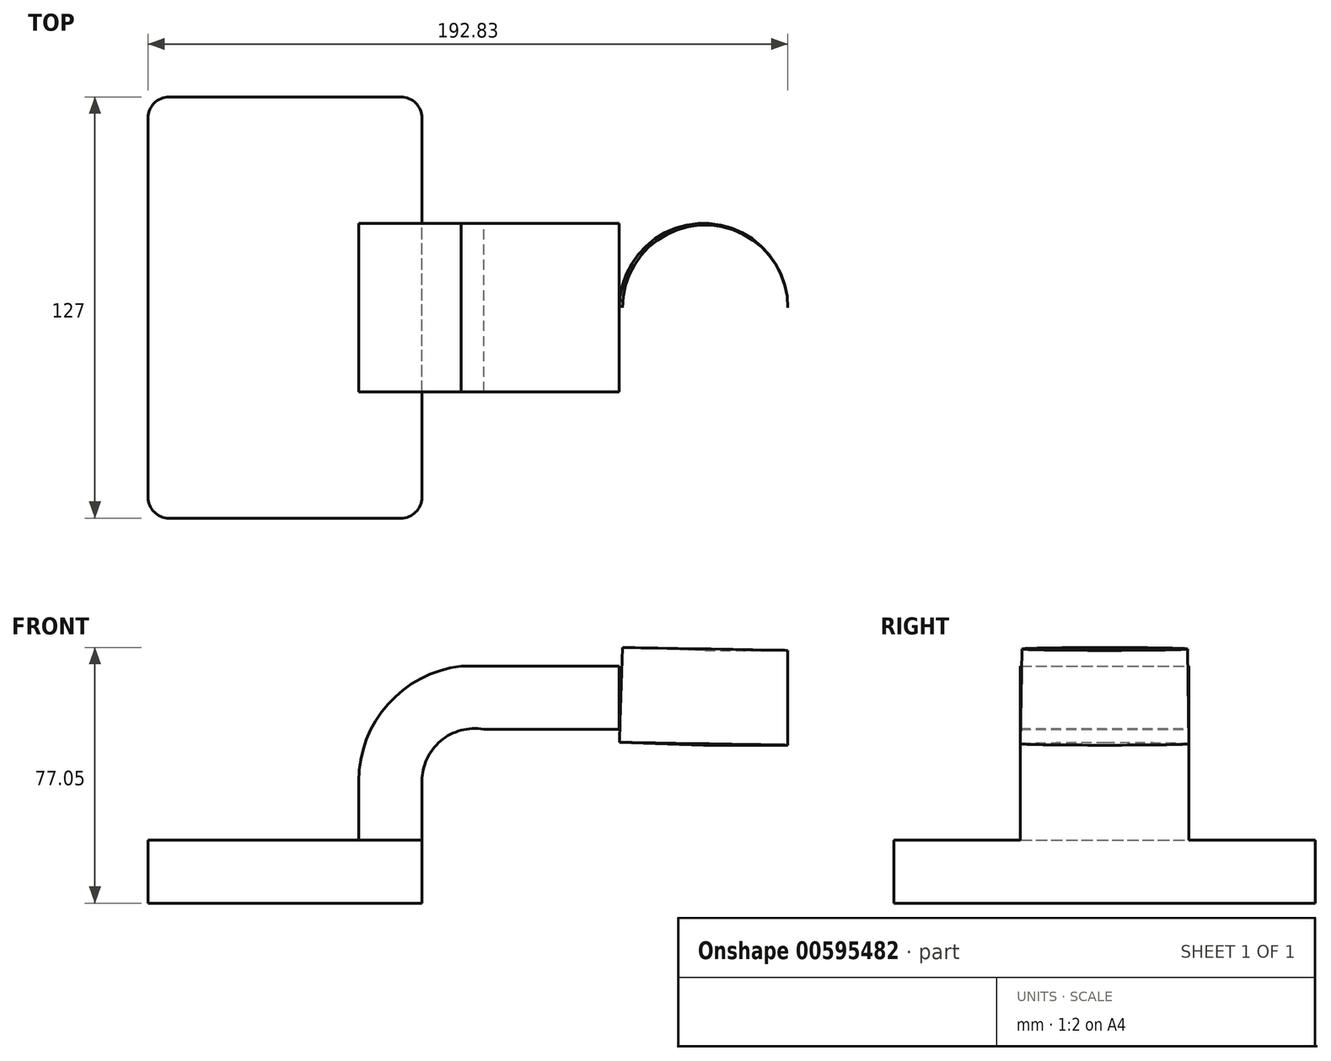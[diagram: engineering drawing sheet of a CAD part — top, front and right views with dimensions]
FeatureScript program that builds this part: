
annotation { "Feature Type Name" : "Feature", "Feature Type Description" : "" }
export const myFeature = defineFeature(function(context is Context, id is Id, definition is map)
    precondition{}
    {
        {
            var Q0;
            Q0=qCreatedBy(makeId("Front.planeOp"),FACE);
            var sketch = newSketch(context, id + "F0", { "sketchPlane" : qUnion([Q0])});
            skLineSegment(sketch, "E0.bottom", {"start": v(-41.28, -9.53) * mm, "end": v(41.28, -9.53) * mm});
            skLineSegment(sketch, "E0.top", {"start": v(-41.28, 9.53) * mm, "end": v(41.28, 9.53) * mm});
            skLineSegment(sketch, "E0.left", {"start": v(-41.28, -9.53) * mm, "end": v(-41.28, 9.53) * mm});
            skLineSegment(sketch, "E0.right", {"start": v(41.28, -9.53) * mm, "end": v(41.28, 9.53) * mm});
            skPoint(sketch, "E0.middle", {"position": v(0, 0) * mm});
            skLineSegment(sketch, "E1.bottom", {"start": v(100.76, 38.1) * mm, "end": v(151.56, 38.1) * mm});
            skLineSegment(sketch, "E1.top", {"start": v(100.76, 66.68) * mm, "end": v(151.56, 66.68) * mm});
            skLineSegment(sketch, "E1.left", {"start": v(100.76, 38.1) * mm, "end": v(100.76, 66.67) * mm});
            skLineSegment(sketch, "E1.right", {"start": v(151.56, 38.1) * mm, "end": v(151.56, 66.67) * mm});
            skPoint(sketch, "E1.middle", {"position": v(126.16, 52.39) * mm});
            skLineSegment(sketch, "E2", {"start": v(41.28, 9.53) * mm, "end": v(41.28, 27.24) * mm});
            skArc(sketch, "E3", {"start": v(41.28, 27.24) * mm, "mid": v(46.94, 39.4) * mm, "end": v(59.9, 42.88) * mm});
            skLineSegment(sketch, "E4", {"start": v(59.9, 42.88) * mm, "end": v(85.72, 42.88) * mm});
            skLineSegment(sketch, "E5.0", {"start": v(53.08, 61.93) * mm, "end": v(126.64, 61.93) * mm});
            skArc(sketch, "E5.1", {"start": v(22.23, 27.24) * mm, "mid": v(31.05, 50.45) * mm, "end": v(53.08, 61.93) * mm});
            skLineSegment(sketch, "E5.2", {"start": v(22.22, 9.53) * mm, "end": v(22.22, 27.24) * mm});
            skLineSegment(sketch, "E6", {"start": v(85.72, 42.88) * mm, "end": v(126.16, 42.88) * mm});
            skPoint(sketch, "E6.endSnap0", {"position": v(126.16, 38.1) * mm});
            skLineSegment(sketch, "E7", {"start": v(126.16, 38.1) * mm, "end": v(126.64, 66.67) * mm});
            skFitSpline(sketch, "E8", {"points": [v(-41.28, 9.53) * mm, v(53.08, 61.93) * mm], "startDerivative": vector(-0.57, 100.62) * mm, "endDerivative": vector(116.49, 1.83) * mm});
            skSolve(sketch);
        }
        {
            var Q0;
            Q0=makeQuery(id+"F0.imprint","IMPRINT",FACE,{"disambiguationData":[TD([[makeQuery(id+"F0.imprint","IMPRINT",EDGE,{"derivedFrom":sQuery(id+"F0.wireOp",EDGE,"E0.bottom")}),1.0]])]});
            extrude(context, id + "F1", {"entities" : qUnion([Q0]), "endBound" : BoundingType.SYMMETRIC, "depth" : 127 * mm, "offsetDistance" : 25.4 * mm});
        }
        {
            var Q0;
            {var subQ0=sQuery(id+"F0.wireOp",EDGE,"E2");Q0=makeQuery(id+"F0.imprint","IMPRINT",FACE,{"disambiguationData":[TD([[makeQuery(id+"F0.imprint","IMPRINT",EDGE,{"derivedFrom":subQ0}),1.0]])]});}
            extrude(context, id + "F2", {"entities" : qUnion([Q0]), "operationType" : NewBodyOperationType.ADD, "endBound" : BoundingType.SYMMETRIC, "depth" : 50.8 * mm, "offsetDistance" : 25.4 * mm});
        }
        {
            var Q0;
            Q0=makeQuery(id+"F0.imprint","IMPRINT",FACE,{"disambiguationData":[TD([[makeQuery(id+"F0.imprint","IMPRINT",EDGE,{"derivedFrom":sQuery(id+"F0.wireOp",EDGE,"E5.1")}),1.0]])]});
            extrude(context, id + "F3", {"entities" : qUnion([Q0]), "operationType" : NewBodyOperationType.ADD, "endBound" : BoundingType.SYMMETRIC, "depth" : 15.88 * mm, "offsetDistance" : 25.4 * mm});
        }
        {
            var Q0;
            {var subQ0=sQuery(id+"F0.wireOp",EDGE,"E1.right");Q0=makeQuery(id+"F0.imprint","IMPRINT",FACE,{"disambiguationData":[TD([[makeQuery(id+"F0.imprint","IMPRINT",EDGE,{"derivedFrom":subQ0}),1.0]])]});}
            var Q1;
            Q1=sQuery(id+"F0.wireOp",EDGE,"E7");
            revolve(context, id + "F4", {"entities" : qUnion([Q0]), "axis" : qUnion([Q1]), "revolveType" : RevolveType.FULL});
        }
        {
            var Q0;
            Q0=makeQuery(id+"F1.opExtrude","CAP_EDGE",EDGE,{"disambiguationData":[OSD([sQuery(id+"F0.wireOp",EDGE,"E0.left")])],"isStart":false});
            var Q1;
            Q1=makeQuery(id+"F1.opExtrude","CAP_EDGE",EDGE,{"disambiguationData":[OSD([sQuery(id+"F0.wireOp",EDGE,"E0.right")])],"isStart":false});
            var Q2;
            Q2=makeQuery(id+"F1.opExtrude","CAP_EDGE",EDGE,{"disambiguationData":[OSD([sQuery(id+"F0.wireOp",EDGE,"E0.right")])],"isStart":true});
            var Q3;
            Q3=makeQuery(id+"F1.opExtrude","CAP_EDGE",EDGE,{"disambiguationData":[OSD([sQuery(id+"F0.wireOp",EDGE,"E0.left")])],"isStart":true});
            fillet(context, id + "F5", {"entities" : qUnion([Q0, Q1, Q2, Q3]), "radius" : 6.35 * mm, "tangentPropagation" : true, "allowEdgeOverflow" : false});
        }
    });
